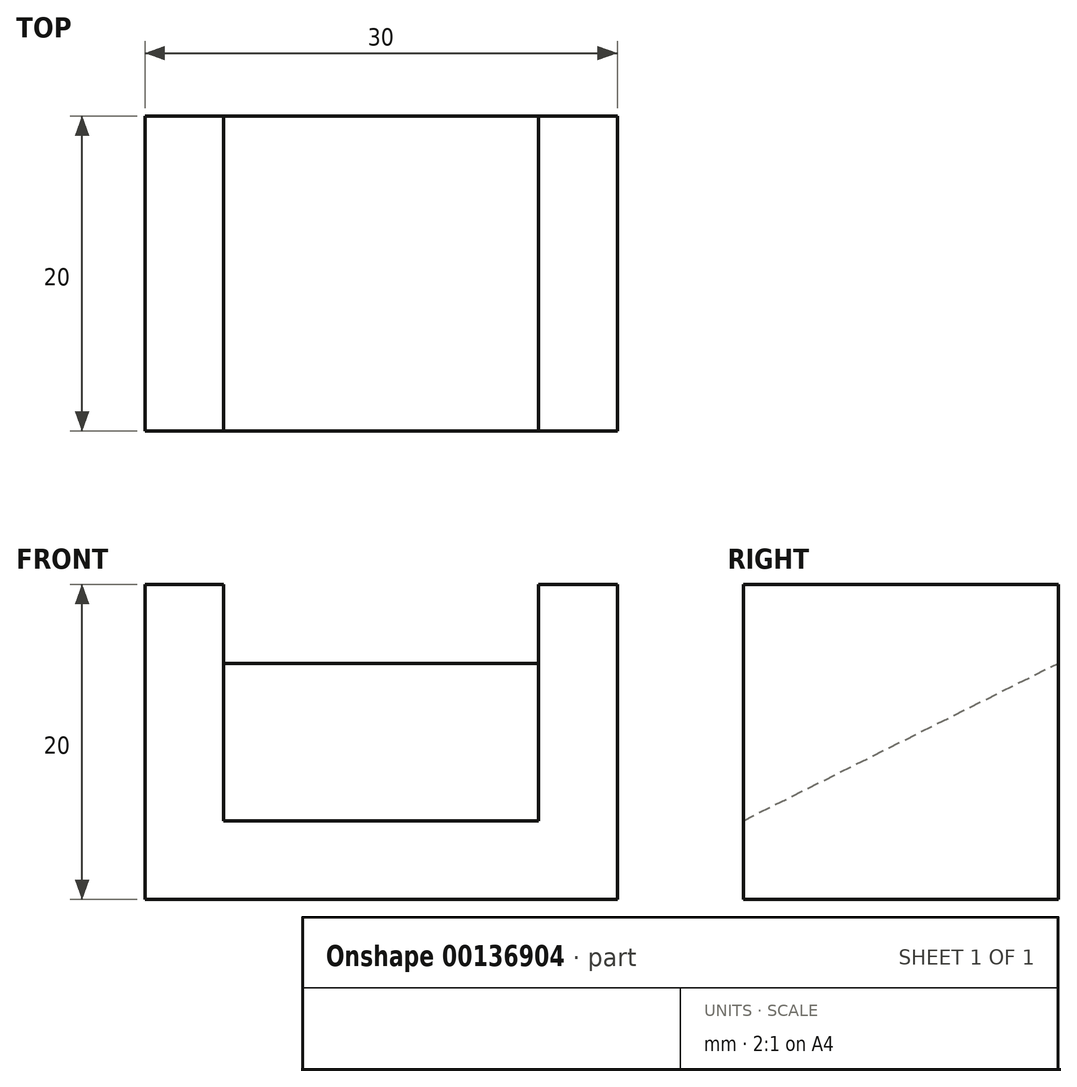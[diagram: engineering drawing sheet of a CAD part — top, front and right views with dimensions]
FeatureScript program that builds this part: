
annotation { "Feature Type Name" : "Feature", "Feature Type Description" : "" }
export const myFeature = defineFeature(function(context is Context, id is Id, definition is map)
    precondition{}
    {
        {
            var Q0;
            Q0=qCreatedBy(makeId("Right.planeOp"),FACE);
            var sketch = newSketch(context, id + "F0", { "sketchPlane" : qUnion([Q0])});
            skLineSegment(sketch, "E0.bottom", {"start": v(0, 0) * mm, "end": v(0, 0) * mm});
            skLineSegment(sketch, "E1", {"start": v(0, 0) * mm, "end": v(0, 20) * mm});
            skLineSegment(sketch, "E2", {"start": v(0, 20) * mm, "end": v(20, 20) * mm});
            skLineSegment(sketch, "E3", {"start": v(20, 20) * mm, "end": v(20, 0) * mm});
            skLineSegment(sketch, "E4", {"start": v(20, 0) * mm, "end": v(0, 0) * mm});
            skSolve(sketch);
        }
        {
            var Q0;
            Q0 = qSketchRegion(id + "F0", true);
            extrude(context, id + "F1", {"entities" : qUnion([Q0]), "depth" : 30 * mm});
        }
        {
            var Q0;
            Q0=makeQuery(id+"F1.opExtrude","CAP_FACE",FACE,{"disambiguationData":[OSD([sQuery(id+"F0.wireOp",EDGE,"E1"),sQuery(id+"F0.wireOp",EDGE,"E2"),sQuery(id+"F0.wireOp",EDGE,"E3"),sQuery(id+"F0.wireOp",EDGE,"E4")])],"isStart":true});
            var sketch = newSketch(context, id + "F2", { "sketchPlane" : qUnion([Q0])});
            skLineSegment(sketch, "E5", {"start": v(-20, 15) * mm, "end": v(0, 5) * mm});
            skLineSegment(sketch, "E6", {"start": v(0, 5) * mm, "end": v(0, 20) * mm});
            skLineSegment(sketch, "E7", {"start": v(0, 20) * mm, "end": v(-20, 20) * mm});
            skLineSegment(sketch, "E8", {"start": v(-20, 20) * mm, "end": v(-20, 15) * mm});
            skSolve(sketch);
        }
        {
            var Q0;
            Q0 = qSketchRegion(id + "F2", true);
            extrude(context, id + "F3", {"entities" : qUnion([Q0]), "operationType" : NewBodyOperationType.REMOVE, "endBound" : BoundingType.SYMMETRIC, "oppositeDirection" : true, "depth" : 70 * mm});
        }
        {
            var Q0;
            Q0=makeQuery(id+"F1.opExtrude","SWEPT_FACE",FACE,{"disambiguationData":[OSD([sQuery(id+"F0.wireOp",EDGE,"E4")])]});
            var sketch = newSketch(context, id + "F4", { "sketchPlane" : qUnion([Q0])});
            skLineSegment(sketch, "E9", {"start": v(0, -20) * mm, "end": v(5, -20) * mm});
            skLineSegment(sketch, "E10", {"start": v(5, -20) * mm, "end": v(5, 0) * mm});
            skLineSegment(sketch, "E11", {"start": v(5, 0) * mm, "end": v(0, 0) * mm});
            skLineSegment(sketch, "E12", {"start": v(0, 0) * mm, "end": v(0, -20) * mm});
            skSolve(sketch);
        }
        {
            var Q0;
            Q0 = qSketchRegion(id + "F4", true);
            extrude(context, id + "F5", {"entities" : qUnion([Q0]), "operationType" : NewBodyOperationType.ADD, "oppositeDirection" : true, "depth" : 20 * mm});
        }
        {
            var Q0;
            Q0=makeQuery(id+"F1.opExtrude","SWEPT_FACE",FACE,{"disambiguationData":[OSD([sQuery(id+"F0.wireOp",EDGE,"E4")])]});
            var sketch = newSketch(context, id + "F6", { "sketchPlane" : qUnion([Q0])});
            skLineSegment(sketch, "E13", {"start": v(30, -20) * mm, "end": v(30, 0) * mm});
            skLineSegment(sketch, "E14", {"start": v(30, 0) * mm, "end": v(25, 0) * mm});
            skLineSegment(sketch, "E15", {"start": v(25, 0) * mm, "end": v(25, -20) * mm});
            skLineSegment(sketch, "E16", {"start": v(25, -20) * mm, "end": v(30, -20) * mm});
            skSolve(sketch);
        }
        {
            var Q0;
            Q0 = qSketchRegion(id + "F6", true);
            extrude(context, id + "F7", {"entities" : qUnion([Q0]), "operationType" : NewBodyOperationType.ADD, "oppositeDirection" : true, "depth" : 20 * mm});
        }
    });
